# Revit family: P6828
name_source: partatom
category: Lighting Fixtures
revit_build: Autodesk Revit 2014 (Build: 20130308_1515(x64)
units: mm (PartAtom-declared; Revit-internal decimal feet)

## types (1)
- P6828
    Apparent Load = 5 VA
    Assembly Code = D5020200
    Color Filter = 16777215
    Connector Description = Lighting Connector
    Default Elevation = 48"
    Description = The P6827 and P6828 LED Step Lights are ideal for a wide variety of interior and exterior
applications including residential and. commercial. The Step Lights feature a 120V alternating current source and eliminates the need for a traditional LED driver. This modular
approach results in an encapsulated luminaire that unites performance, cost and safety
benefits
    Dimming Lamp Color Temperature Shift = <None>
    Emit Shape Visible in Rendering = No
    Emit from Rectangle Length = 3/8"
    Emit from Rectangle Width = 1"
    Features = Available in Brushed Nickel (-09), Antique Bronze (-20), White (-30), Black (-31)
• Heavy Steel construction
• Vertical and horizontal louver design
• Horizontal mounting on a single gang recessed wallbox (2” min. clearance)
    Housing Material = Paint - Hubbell - Light Silver
    Lamp = LED
    Length = 3"
    Load Classification = Lighting
    Manufacturer = Progress Lighting
    Model = P6828
    Photometric Web File = PROG_P6828_15.00135 Series_testlabreports.ies
    Power Factor = 1
    Product Documentation Link = https://hubbellcdn.com
    Product URL = https://www.hubbell.com
    Raidus = 45 1/8"
    Reflector Finish = Hubbell - White Glass
    Tilt Angle = 60.00°
    URL = https://www.hubbell.com
    Vertical Louver = Yes
    Voltage = 120 V
    Warranty = 5 years Warranty
    Wattage Comments = Variable Intensity technology provides specifiable lumen output/wattage
    Watts = 5 W
    Width = 4 7/8"

## geometry (parser evidence)
native form markers: Blend x20, Sweep x1
no freeform markers — native parametric forms only
